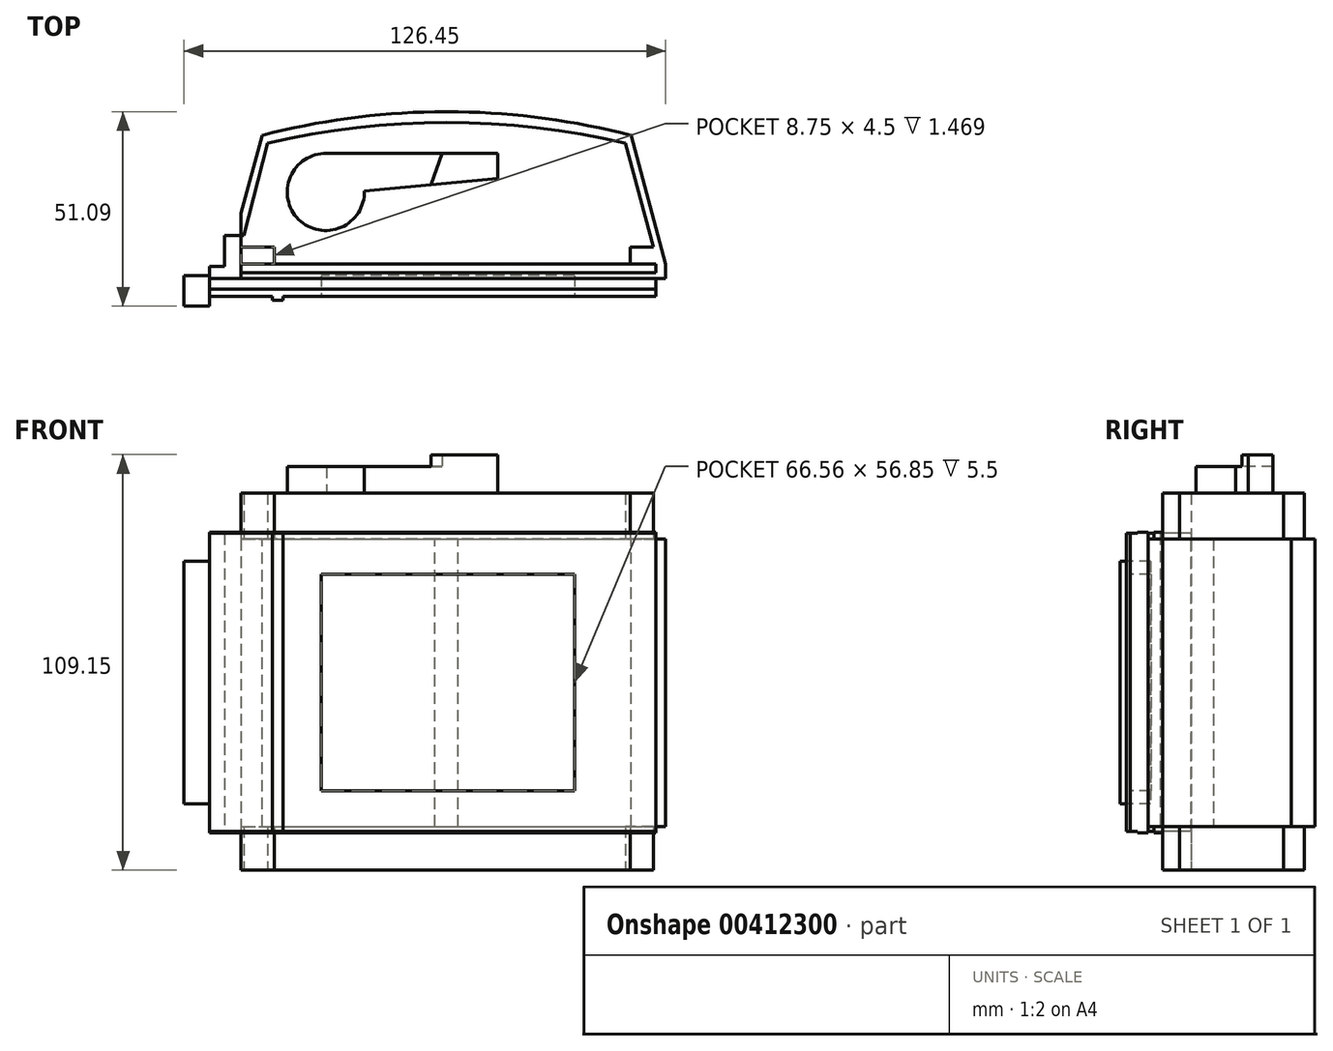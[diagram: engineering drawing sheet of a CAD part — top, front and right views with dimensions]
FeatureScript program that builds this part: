
annotation { "Feature Type Name" : "Feature", "Feature Type Description" : "" }
export const myFeature = defineFeature(function(context is Context, id is Id, definition is map)
    precondition{}
    {
        {
            var Q0;
            Q0=qCreatedBy(makeId("Front.planeOp"),FACE);
            var sketch = newSketch(context, id + "F0", { "sketchPlane" : qUnion([Q0])});
            skLineSegment(sketch, "E0.bottom", {"start": v(58.63, 39.17) * mm, "end": v(-58.62, 39.17) * mm});
            skLineSegment(sketch, "E0.top", {"start": v(58.63, -39.17) * mm, "end": v(-58.63, -39.17) * mm});
            skLineSegment(sketch, "E0.left", {"start": v(58.63, 39.17) * mm, "end": v(58.63, -39.18) * mm});
            skLineSegment(sketch, "E0.right", {"start": v(-58.63, 39.17) * mm, "end": v(-58.63, -39.17) * mm});
            skPoint(sketch, "E0.middle", {"position": v(0, 0) * mm});
            skLineSegment(sketch, "E1.bottom", {"start": v(-39.38, 39.17) * mm, "end": v(-41.87, 39.17) * mm});
            skLineSegment(sketch, "E1.top", {"start": v(-39.38, -39.17) * mm, "end": v(-41.87, -39.17) * mm});
            skLineSegment(sketch, "E1.left", {"start": v(-39.38, 39.18) * mm, "end": v(-39.38, -39.17) * mm});
            skLineSegment(sketch, "E1.right", {"start": v(-41.87, 39.18) * mm, "end": v(-41.87, -39.17) * mm});
            skSolve(sketch);
        }
        {
            var Q0;
            Q0 = qSketchRegion(id + "F0", true);
            extrude(context, id + "F1", {"entities" : qUnion([Q0]), "depth" : 4.75 * mm});
        }
        {
            var Q0;
            Q0=makeQuery(id+"F1.opExtrude","CAP_FACE",FACE,{"disambiguationData":[OSD([sQuery(id+"F0.wireOp",EDGE,"E0.bottom"),sQuery(id+"F0.wireOp",EDGE,"E0.top"),sQuery(id+"F0.wireOp",EDGE,"E0.left"),sQuery(id+"F0.wireOp",EDGE,"E0.right"),sQuery(id+"F0.wireOp",EDGE,"E1.bottom"),sQuery(id+"F0.wireOp",EDGE,"E1.top")])],"isStart":false});
            var sketch = newSketch(context, id + "F2", { "sketchPlane" : qUnion([Q0])});
            skLineSegment(sketch, "E2.bottom", {"start": v(-42.12, 39.17) * mm, "end": v(-39.38, 39.17) * mm});
            skLineSegment(sketch, "E2.top", {"start": v(-42.12, -39.17) * mm, "end": v(-39.38, -39.17) * mm});
            skLineSegment(sketch, "E2.left", {"start": v(-42.12, 39.17) * mm, "end": v(-42.12, -39.17) * mm});
            skLineSegment(sketch, "E2.right", {"start": v(-39.38, 39.17) * mm, "end": v(-39.38, -39.17) * mm});
            skSolve(sketch);
        }
        {
            var Q0;
            Q0 = qSketchRegion(id + "F2", true);
            extrude(context, id + "F3", {"entities" : qUnion([Q0]), "operationType" : NewBodyOperationType.ADD, "depth" : 1 * mm});
        }
        {
            var Q0;
            {var subQ0=sQuery(id+"F0.wireOp",EDGE,"E0.left");var subQ1=sQuery(id+"F0.wireOp",EDGE,"E1.top");var subQ2=sQuery(id+"F0.wireOp",EDGE,"E0.top");var subQ3=sQuery(id+"F0.wireOp",EDGE,"E1.bottom");var subQ4=sQuery(id+"F0.wireOp",EDGE,"E0.bottom");Q0=makeQuery(id+"F3.boolean.opBoolean","SPLIT",FACE,{"disambiguationData":[TD([makeQuery(id+"F1.opExtrude","SWEPT_FACE",FACE,{"disambiguationData":[OSD([subQ0])]})])],"derivedFrom":makeQuery(id+"F1.opExtrude","CAP_FACE",FACE,{"disambiguationData":[OSD([subQ4,subQ2,subQ0,sQuery(id+"F0.wireOp",EDGE,"E0.right"),subQ3,subQ1])],"isStart":false})});}
            var sketch = newSketch(context, id + "F4", { "sketchPlane" : qUnion([Q0])});
            skLineSegment(sketch, "E3.bottom", {"start": v(37.23, 28.42) * mm, "end": v(-29.34, 28.42) * mm});
            skLineSegment(sketch, "E3.top", {"start": v(37.23, -28.42) * mm, "end": v(-29.33, -28.42) * mm});
            skLineSegment(sketch, "E3.left", {"start": v(37.23, 28.42) * mm, "end": v(37.23, -28.42) * mm});
            skLineSegment(sketch, "E3.right", {"start": v(-29.34, 28.42) * mm, "end": v(-29.33, -28.42) * mm});
            skSolve(sketch);
        }
        {
            var Q0;
            Q0 = qSketchRegion(id + "F4", true);
            extrude(context, id + "F5", {"entities" : qUnion([Q0]), "operationType" : NewBodyOperationType.REMOVE, "oppositeDirection" : true, "depth" : 25 * mm});
        }
        {
            var Q0;
            Q0=makeQuery(id+"F1.opExtrude","CAP_FACE",FACE,{"disambiguationData":[OSD([sQuery(id+"F0.wireOp",EDGE,"E0.bottom"),sQuery(id+"F0.wireOp",EDGE,"E0.top"),sQuery(id+"F0.wireOp",EDGE,"E0.left"),sQuery(id+"F0.wireOp",EDGE,"E0.right"),sQuery(id+"F0.wireOp",EDGE,"E1.bottom"),sQuery(id+"F0.wireOp",EDGE,"E1.top")])],"isStart":true});
            var sketch = newSketch(context, id + "F6", { "sketchPlane" : qUnion([Q0])});
            skLineSegment(sketch, "E4.bottom", {"start": v(58.63, 39.5) * mm, "end": v(-58.63, 39.5) * mm});
            skLineSegment(sketch, "E4.top", {"start": v(58.63, -39.5) * mm, "end": v(-58.63, -39.5) * mm});
            skLineSegment(sketch, "E4.left", {"start": v(58.63, 39.5) * mm, "end": v(58.63, -39.5) * mm});
            skLineSegment(sketch, "E4.right", {"start": v(-58.63, 39.5) * mm, "end": v(-58.63, -39.5) * mm});
            skPoint(sketch, "E4.middle", {"position": v(0, 0) * mm});
            skSolve(sketch);
        }
        {
            var Q0;
            Q0 = qSketchRegion(id + "F6", true);
            extrude(context, id + "F7", {"entities" : qUnion([Q0]), "operationType" : NewBodyOperationType.ADD, "oppositeDirection" : true, "depth" : 2.86 * mm});
        }
        {
            var Q0;
            {var subQ0=sQuery(id+"F0.wireOp",EDGE,"E0.right");var subQ1=sQuery(id+"F0.wireOp",EDGE,"E1.top");var subQ2=sQuery(id+"F0.wireOp",EDGE,"E0.top");var subQ3=sQuery(id+"F0.wireOp",EDGE,"E1.bottom");var subQ4=sQuery(id+"F0.wireOp",EDGE,"E0.bottom");Q0=makeQuery(id+"F3.boolean.opBoolean","SPLIT",FACE,{"disambiguationData":[TD([makeQuery(id+"F1.opExtrude","SWEPT_FACE",FACE,{"disambiguationData":[OSD([subQ0])]})])],"derivedFrom":makeQuery(id+"F1.opExtrude","CAP_FACE",FACE,{"disambiguationData":[OSD([subQ4,subQ2,sQuery(id+"F0.wireOp",EDGE,"E0.left"),subQ0,subQ3,subQ1])],"isStart":false})});}
            var sketch = newSketch(context, id + "F8", { "sketchPlane" : qUnion([Q0])});
            skLineSegment(sketch, "E5.bottom", {"start": v(-58.62, 39.17) * mm, "end": v(-54.72, 39.17) * mm});
            skLineSegment(sketch, "E5.top", {"start": v(-58.62, -39.17) * mm, "end": v(-54.72, -39.17) * mm});
            skLineSegment(sketch, "E5.left", {"start": v(-58.62, 39.17) * mm, "end": v(-58.62, -39.17) * mm});
            skLineSegment(sketch, "E5.right", {"start": v(-54.72, 39.17) * mm, "end": v(-54.72, -39.17) * mm});
            skSolve(sketch);
        }
        {
            var Q0;
            Q0 = qSketchRegion(id + "F8", true);
            extrude(context, id + "F9", {"entities" : qUnion([Q0]), "operationType" : NewBodyOperationType.ADD, "oppositeDirection" : true, "depth" : 7.9 * mm});
        }
        {
            var Q0;
            {var subQ0=sQuery(id+"F0.wireOp",EDGE,"E0.right");var subQ1=sQuery(id+"F0.wireOp",EDGE,"E1.top");var subQ2=sQuery(id+"F0.wireOp",EDGE,"E0.top");var subQ3=sQuery(id+"F0.wireOp",EDGE,"E1.bottom");var subQ4=sQuery(id+"F0.wireOp",EDGE,"E0.bottom");Q0=makeQuery(id+"F3.boolean.opBoolean","SPLIT",FACE,{"disambiguationData":[TD([makeQuery(id+"F1.opExtrude","SWEPT_FACE",FACE,{"disambiguationData":[OSD([subQ0])]})])],"derivedFrom":makeQuery(id+"F1.opExtrude","CAP_FACE",FACE,{"disambiguationData":[OSD([subQ4,subQ2,sQuery(id+"F0.wireOp",EDGE,"E0.left"),subQ0,subQ3,subQ1])],"isStart":false})});}
            var sketch = newSketch(context, id + "F10", { "sketchPlane" : qUnion([Q0])});
            skLineSegment(sketch, "E6.bottom", {"start": v(-58.62, 39.17) * mm, "end": v(-50.31, 39.17) * mm});
            skLineSegment(sketch, "E6.top", {"start": v(-58.62, -39.17) * mm, "end": v(-50.31, -39.17) * mm});
            skLineSegment(sketch, "E6.left", {"start": v(-58.62, 39.17) * mm, "end": v(-58.62, -39.17) * mm});
            skLineSegment(sketch, "E6.right", {"start": v(-50.31, 39.17) * mm, "end": v(-50.31, -39.17) * mm});
            skSolve(sketch);
        }
        {
            var Q0;
            Q0 = qSketchRegion(id + "F10", true);
            extrude(context, id + "F11", {"entities" : qUnion([Q0]), "operationType" : NewBodyOperationType.ADD, "oppositeDirection" : true, "depth" : 6.5 * mm});
        }
        {
            var Q0;
            Q0=makeQuery(id+"F7.boolean.opBoolean","MERGE",FACE,{"derivedFrom":[makeQuery(id+"F1.opExtrude","CAP_FACE",FACE,{"disambiguationData":[OSD([sQuery(id+"F0.wireOp",EDGE,"E0.bottom"),sQuery(id+"F0.wireOp",EDGE,"E0.top"),sQuery(id+"F0.wireOp",EDGE,"E0.left"),sQuery(id+"F0.wireOp",EDGE,"E0.right"),sQuery(id+"F0.wireOp",EDGE,"E1.bottom"),sQuery(id+"F0.wireOp",EDGE,"E1.top")])],"isStart":true}),makeQuery(id+"F7.opExtrude","CAP_FACE",FACE,{"disambiguationData":[OSD([sQuery(id+"F6.wireOp",EDGE,"E4.bottom"),sQuery(id+"F6.wireOp",EDGE,"E4.top"),sQuery(id+"F6.wireOp",EDGE,"E4.left"),sQuery(id+"F6.wireOp",EDGE,"E4.right")])],"isStart":true})]});
            var sketch = newSketch(context, id + "F12", { "sketchPlane" : qUnion([Q0])});
            skLineSegment(sketch, "E7.left", {"start": v(-61.13, 37.7) * mm, "end": v(-61.13, -37.83) * mm});
            skLineSegment(sketch, "E8", {"start": v(50.31, 37.7) * mm, "end": v(50.31, -37.83) * mm});
            skLineSegment(sketch, "E9", {"start": v(50.31, -37.83) * mm, "end": v(-61.13, -37.83) * mm});
            skLineSegment(sketch, "E10", {"start": v(50.31, 37.7) * mm, "end": v(-61.13, 37.7) * mm});
            skSolve(sketch);
        }
        {
            var Q0;
            Q0 = qSketchRegion(id + "F12", true);
            extrude(context, id + "F13", {"entities" : qUnion([Q0]), "operationType" : NewBodyOperationType.ADD, "depth" : 1.5 * mm});
        }
        {
            var Q0;
            Q0=makeQuery(id+"F11.opExtrude","CAP_FACE",FACE,{"disambiguationData":[OSD([sQuery(id+"F10.wireOp",EDGE,"E6.bottom"),sQuery(id+"F10.wireOp",EDGE,"E6.top"),sQuery(id+"F10.wireOp",EDGE,"E6.left"),sQuery(id+"F10.wireOp",EDGE,"E6.right")])],"isStart":false});
            var sketch = newSketch(context, id + "F14", { "sketchPlane" : qUnion([Q0])});
            skLineSegment(sketch, "E11.bottom", {"start": v(54.72, 39.17) * mm, "end": v(50.31, 39.17) * mm});
            skLineSegment(sketch, "E11.top", {"start": v(54.72, -39.17) * mm, "end": v(50.31, -39.17) * mm});
            skLineSegment(sketch, "E11.left", {"start": v(54.72, 39.17) * mm, "end": v(54.72, -39.17) * mm});
            skLineSegment(sketch, "E11.right", {"start": v(50.31, 39.17) * mm, "end": v(50.31, -39.17) * mm});
            skSolve(sketch);
        }
        {
            var Q0;
            Q0 = qSketchRegion(id + "F14", true);
            extrude(context, id + "F15", {"entities" : qUnion([Q0]), "operationType" : NewBodyOperationType.ADD, "depth" : 9.5 * mm});
        }
        {
            var Q0;
            Q0=makeQuery(id+"F13.opExtrude","CAP_FACE",FACE,{"disambiguationData":[OSD([sQuery(id+"F12.wireOp",EDGE,"E7.left"),sQuery(id+"F12.wireOp",EDGE,"E8"),sQuery(id+"F12.wireOp",EDGE,"E9"),sQuery(id+"F12.wireOp",EDGE,"E10")])],"isStart":false});
            var sketch = newSketch(context, id + "F16", { "sketchPlane" : qUnion([Q0])});
            skLineSegment(sketch, "E12", {"start": v(-58.63, 39.5) * mm, "end": v(50.31, 39.5) * mm});
            skLineSegment(sketch, "E13", {"start": v(50.31, 39.5) * mm, "end": v(50.31, -39.5) * mm});
            skLineSegment(sketch, "E14", {"start": v(50.31, -39.5) * mm, "end": v(-58.63, -39.5) * mm});
            skLineSegment(sketch, "E15", {"start": v(-58.63, -39.5) * mm, "end": v(-58.63, -37.83) * mm});
            skLineSegment(sketch, "E16", {"start": v(-58.63, -37.83) * mm, "end": v(-61.13, -37.83) * mm});
            skLineSegment(sketch, "E17", {"start": v(-61.13, -37.83) * mm, "end": v(-61.13, 37.7) * mm});
            skLineSegment(sketch, "E18", {"start": v(-61.13, 37.7) * mm, "end": v(-58.63, 37.7) * mm});
            skLineSegment(sketch, "E19", {"start": v(-58.63, 37.7) * mm, "end": v(-58.63, 39.5) * mm});
            skSolve(sketch);
        }
        {
            var Q0;
            Q0 = qSketchRegion(id + "F16", true);
            extrude(context, id + "F17", {"entities" : qUnion([Q0]), "operationType" : NewBodyOperationType.ADD, "depth" : 2.25 * mm});
        }
        {
            var Q0;
            Q0=makeQuery(id+"F17.opExtrude","CAP_FACE",FACE,{"disambiguationData":[OSD([sQuery(id+"F16.wireOp",EDGE,"E12"),sQuery(id+"F16.wireOp",EDGE,"E13"),sQuery(id+"F16.wireOp",EDGE,"E14"),sQuery(id+"F16.wireOp",EDGE,"E15"),sQuery(id+"F16.wireOp",EDGE,"E16"),sQuery(id+"F16.wireOp",EDGE,"E17"),sQuery(id+"F16.wireOp",EDGE,"E18"),sQuery(id+"F16.wireOp",EDGE,"E19")])],"isStart":false});
            var sketch = newSketch(context, id + "F18", { "sketchPlane" : qUnion([Q0])});
            skLineSegment(sketch, "E20", {"start": v(-61.13, 37.7) * mm, "end": v(-58.63, 37.7) * mm});
            skLineSegment(sketch, "E21", {"start": v(-58.63, -37.83) * mm, "end": v(-61.13, -37.83) * mm});
            skLineSegment(sketch, "E22", {"start": v(-61.13, -37.83) * mm, "end": v(-61.13, 37.7) * mm});
            skLineSegment(sketch, "E23", {"start": v(-58.63, 37.7) * mm, "end": v(50.31, 37.7) * mm});
            skLineSegment(sketch, "E24", {"start": v(-58.63, -37.83) * mm, "end": v(50.31, -37.83) * mm});
            skLineSegment(sketch, "E25", {"start": v(50.31, -37.83) * mm, "end": v(50.31, 37.7) * mm});
            skSolve(sketch);
        }
        {
            var Q0;
            Q0 = qSketchRegion(id + "F18", true);
            extrude(context, id + "F19", {"entities" : qUnion([Q0]), "operationType" : NewBodyOperationType.ADD, "depth" : 40 * mm});
        }
        {
            var Q0;
            Q0=makeQuery(id+"F19.boolean.opBoolean","MERGE",FACE,{"derivedFrom":[makeQuery(id+"F17.boolean.opBoolean","MERGE",FACE,{"derivedFrom":[makeQuery(id+"F13.opExtrude","SWEPT_FACE",FACE,{"disambiguationData":[OSD([sQuery(id+"F12.wireOp",EDGE,"E10")])]}),makeQuery(id+"F17.opExtrude","SWEPT_FACE",FACE,{"disambiguationData":[OSD([sQuery(id+"F16.wireOp",EDGE,"E18")])]})]}),makeQuery(id+"F19.opExtrude","SWEPT_FACE",FACE,{"disambiguationData":[OSD([sQuery(id+"F18.wireOp",EDGE,"E20"),sQuery(id+"F18.wireOp",EDGE,"E23")])]})]});
            var sketch = newSketch(context, id + "F20", { "sketchPlane" : qUnion([Q0])});
            skLineSegment(sketch, "E26", {"start": v(61.13, 3.75) * mm, "end": v(52.07, 37.56) * mm});
            skLineSegment(sketch, "E27", {"start": v(52.07, 37.56) * mm, "end": v(-44.84, 37.56) * mm, "construction": true});
            skLineSegment(sketch, "E28", {"start": v(-44.84, 37.56) * mm, "end": v(-51.88, 11.25) * mm});
            skLineSegment(sketch, "E29", {"start": v(-51.88, 11.25) * mm, "end": v(-55.7, 49.97) * mm});
            skLineSegment(sketch, "E30", {"start": v(-55.7, 49.97) * mm, "end": v(71.24, 49.97) * mm});
            skLineSegment(sketch, "E31", {"start": v(71.24, 49.97) * mm, "end": v(61.13, 3.75) * mm});
            skLineSegment(sketch, "E32", {"start": v(-51.88, 11.25) * mm, "end": v(59.12, 11.25) * mm, "construction": true});
            skLineSegment(sketch, "E33", {"start": v(3.62, 11.25) * mm, "end": v(3.62, 37.56) * mm, "construction": true});
            skArc(sketch, "E34", {"start": v(52.07, 37.56) * mm, "mid": v(3.62, 43.77) * mm, "end": v(-44.84, 37.56) * mm});
            skSolve(sketch);
        }
        {
            var Q0;
            Q0 = qSketchRegion(id + "F20", true);
            extrude(context, id + "F21", {"entities" : qUnion([Q0]), "operationType" : NewBodyOperationType.REMOVE, "oppositeDirection" : true, "depth" : 95.3 * mm});
        }
        {
            var Q0;
            Q0=makeQuery(id+"F19.boolean.opBoolean","MERGE",FACE,{"derivedFrom":[makeQuery(id+"F17.boolean.opBoolean","MERGE",FACE,{"derivedFrom":[makeQuery(id+"F13.opExtrude","SWEPT_FACE",FACE,{"disambiguationData":[OSD([sQuery(id+"F12.wireOp",EDGE,"E10")])]}),makeQuery(id+"F17.opExtrude","SWEPT_FACE",FACE,{"disambiguationData":[OSD([sQuery(id+"F16.wireOp",EDGE,"E18")])]})]}),makeQuery(id+"F19.opExtrude","SWEPT_FACE",FACE,{"disambiguationData":[OSD([sQuery(id+"F18.wireOp",EDGE,"E20"),sQuery(id+"F18.wireOp",EDGE,"E23")])]})]});
            var sketch = newSketch(context, id + "F22", { "sketchPlane" : qUnion([Q0])});
            skLineSegment(sketch, "E35", {"start": v(-41.56, 3.75) * mm, "end": v(-41.56, 8.25) * mm, "construction": true});
            skLineSegment(sketch, "E36", {"start": v(51.92, 8.25) * mm, "end": v(51.92, 3.75) * mm, "construction": true});
            skLineSegment(sketch, "E37", {"start": v(-50.31, 8.25) * mm, "end": v(-41.56, 8.25) * mm, "construction": true});
            skLineSegment(sketch, "E38", {"start": v(50.6, 35.56) * mm, "end": v(57.92, 8.25) * mm, "construction": true});
            skLineSegment(sketch, "E39", {"start": v(51.92, 8.25) * mm, "end": v(57.92, 8.25) * mm, "construction": true});
            skArc(sketch, "E40", {"start": v(50.6, 35.56) * mm, "mid": v(3.63, 40.98) * mm, "end": v(-43.35, 35.56) * mm, "construction": true});
            skLineSegment(sketch, "E41", {"start": v(-41.57, 3.75) * mm, "end": v(51.92, 3.75) * mm, "construction": true});
            skLineSegment(sketch, "E42", {"start": v(-50.31, 8.25) * mm, "end": v(-41.56, 8.25) * mm});
            skLineSegment(sketch, "E43", {"start": v(-41.56, 8.25) * mm, "end": v(-41.56, 3.75) * mm});
            skLineSegment(sketch, "E44", {"start": v(-41.57, 3.75) * mm, "end": v(51.92, 3.75) * mm});
            skLineSegment(sketch, "E45", {"start": v(51.92, 3.75) * mm, "end": v(51.92, 8.25) * mm});
            skLineSegment(sketch, "E46", {"start": v(51.92, 8.25) * mm, "end": v(57.92, 8.25) * mm});
            skLineSegment(sketch, "E47", {"start": v(57.92, 8.25) * mm, "end": v(50.6, 35.56) * mm});
            skArc(sketch, "E48", {"start": v(50.6, 35.56) * mm, "mid": v(3.63, 40.94) * mm, "end": v(-43.35, 35.56) * mm});
            skLineSegment(sketch, "E49", {"start": v(-50.31, 8.25) * mm, "end": v(-50.31, 11.25) * mm});
            skLineSegment(sketch, "E50", {"start": v(-50.31, 11.25) * mm, "end": v(-49.55, 11.25) * mm});
            skLineSegment(sketch, "E51", {"start": v(-49.55, 11.25) * mm, "end": v(-43.35, 35.56) * mm});
            skSolve(sketch);
        }
        {
            var Q0;
            Q0 = qSketchRegion(id + "F22", true);
            extrude(context, id + "F23", {"entities" : qUnion([Q0]), "operationType" : NewBodyOperationType.ADD, "depth" : 12 * mm, "hasSecondDirection" : true, "secondDirectionOppositeDirection" : true, "secondDirectionDepth" : 87 * mm});
        }
        {
            var Q0;
            Q0=makeQuery(id+"F23.opExtrude","CAP_FACE",FACE,{"disambiguationData":[OSD([sQuery(id+"F22.wireOp",EDGE,"E42"),sQuery(id+"F22.wireOp",EDGE,"E43"),sQuery(id+"F22.wireOp",EDGE,"E44"),sQuery(id+"F22.wireOp",EDGE,"E45"),sQuery(id+"F22.wireOp",EDGE,"E46"),sQuery(id+"F22.wireOp",EDGE,"E47"),sQuery(id+"F22.wireOp",EDGE,"E48"),sQuery(id+"F22.wireOp",EDGE,"E49"),sQuery(id+"F22.wireOp",EDGE,"E50"),sQuery(id+"F22.wireOp",EDGE,"E51")])],"isStart":false});
            var sketch = newSketch(context, id + "F24", { "sketchPlane" : qUnion([Q0])});
            skCircle(sketch, "E52", {"center": v(-28.09, 22.68) * mm, "radius": 10.12 * mm});
            skLineSegment(sketch, "E53", {"start": v(-27.89, 32.8) * mm, "end": v(17.11, 32.8) * mm});
            skLineSegment(sketch, "E54", {"start": v(17.11, 32.8) * mm, "end": v(17.11, 26.3) * mm});
            skLineSegment(sketch, "E55", {"start": v(17.11, 26.3) * mm, "end": v(-17.97, 22.97) * mm});
            skSolve(sketch);
        }
        {
            var Q0;
            Q0 = qSketchRegion(id + "F24", true);
            extrude(context, id + "F25", {"entities" : qUnion([Q0]), "operationType" : NewBodyOperationType.ADD, "depth" : 7 * mm});
        }
        {
            var Q0;
            Q0=makeQuery(id+"F25.opExtrude","CAP_FACE",FACE,{"disambiguationData":[OSD([sQuery(id+"F24.wireOp",EDGE,"E52"),sQuery(id+"F24.wireOp",EDGE,"E53"),sQuery(id+"F24.wireOp",EDGE,"E54"),sQuery(id+"F24.wireOp",EDGE,"E55")])],"isStart":false});
            var sketch = newSketch(context, id + "F26", { "sketchPlane" : qUnion([Q0])});
            skLineSegment(sketch, "E56", {"start": v(17.11, 32.8) * mm, "end": v(2.42, 32.8) * mm});
            skLineSegment(sketch, "E57", {"start": v(2.42, 32.8) * mm, "end": v(-0.43, 24.64) * mm});
            skLineSegment(sketch, "E58", {"start": v(-0.43, 24.64) * mm, "end": v(17.11, 26.3) * mm});
            skLineSegment(sketch, "E59", {"start": v(17.11, 26.3) * mm, "end": v(17.11, 32.8) * mm});
            skSolve(sketch);
        }
        {
            var Q0;
            Q0 = qSketchRegion(id + "F26", true);
            extrude(context, id + "F27", {"entities" : qUnion([Q0]), "operationType" : NewBodyOperationType.ADD, "depth" : 3.15 * mm});
        }
        {
            var Q0;
            Q0=makeQuery(id+"F9.boolean.opBoolean","MERGE",FACE,{"derivedFrom":[makeQuery(id+"F7.boolean.opBoolean","MERGE",FACE,{"derivedFrom":[makeQuery(id+"F1.opExtrude","SWEPT_FACE",FACE,{"disambiguationData":[OSD([sQuery(id+"F0.wireOp",EDGE,"E0.right")])]}),makeQuery(id+"F7.opExtrude","SWEPT_FACE",FACE,{"disambiguationData":[OSD([sQuery(id+"F6.wireOp",EDGE,"E4.left")])]})]}),makeQuery(id+"F9.opExtrude","SWEPT_FACE",FACE,{"disambiguationData":[OSD([sQuery(id+"F8.wireOp",EDGE,"E5.left")])]})]});
            var sketch = newSketch(context, id + "F28", { "sketchPlane" : qUnion([Q0])});
            skLineSegment(sketch, "E60.bottom", {"start": v(-0.66, 31.87) * mm, "end": v(7.34, 31.87) * mm});
            skLineSegment(sketch, "E60.top", {"start": v(-0.66, -31.88) * mm, "end": v(7.34, -31.88) * mm});
            skLineSegment(sketch, "E60.left", {"start": v(-0.66, 31.87) * mm, "end": v(-0.66, -31.88) * mm});
            skLineSegment(sketch, "E60.right", {"start": v(7.34, 31.87) * mm, "end": v(7.34, -31.88) * mm});
            skSolve(sketch);
        }
        {
            var Q0;
            Q0 = qSketchRegion(id + "F28", true);
            extrude(context, id + "F29", {"entities" : qUnion([Q0]), "operationType" : NewBodyOperationType.ADD, "depth" : 6.7 * mm});
        }
        {
            var Q0;
            {var subQ0=sQuery(id+"F0.wireOp",EDGE,"E0.left");var subQ1=sQuery(id+"F0.wireOp",EDGE,"E1.top");var subQ2=sQuery(id+"F0.wireOp",EDGE,"E0.top");var subQ3=sQuery(id+"F0.wireOp",EDGE,"E1.bottom");var subQ4=sQuery(id+"F0.wireOp",EDGE,"E0.bottom");Q0=makeQuery(id+"F3.boolean.opBoolean","SPLIT",FACE,{"disambiguationData":[TD([makeQuery(id+"F1.opExtrude","SWEPT_FACE",FACE,{"disambiguationData":[OSD([subQ0])]})])],"derivedFrom":makeQuery(id+"F1.opExtrude","CAP_FACE",FACE,{"disambiguationData":[OSD([subQ4,subQ2,subQ0,sQuery(id+"F0.wireOp",EDGE,"E0.right"),subQ3,subQ1])],"isStart":false})});}
            var sketch = newSketch(context, id + "F30", { "sketchPlane" : qUnion([Q0])});
            skLineSegment(sketch, "E61.bottom", {"start": v(-29.34, 28.42) * mm, "end": v(37.23, 28.42) * mm});
            skLineSegment(sketch, "E61.top", {"start": v(-29.34, -28.42) * mm, "end": v(37.23, -28.42) * mm});
            skLineSegment(sketch, "E61.left", {"start": v(-29.34, 28.42) * mm, "end": v(-29.34, -28.42) * mm});
            skLineSegment(sketch, "E61.right", {"start": v(37.23, 28.42) * mm, "end": v(37.23, -28.42) * mm});
            skSolve(sketch);
        }
        {
            var Q0;
            Q0 = qSketchRegion(id + "F30", true);
            extrude(context, id + "F31", {"entities" : qUnion([Q0]), "operationType" : NewBodyOperationType.REMOVE, "oppositeDirection" : true, "depth" : 5.5 * mm});
        }
    });
